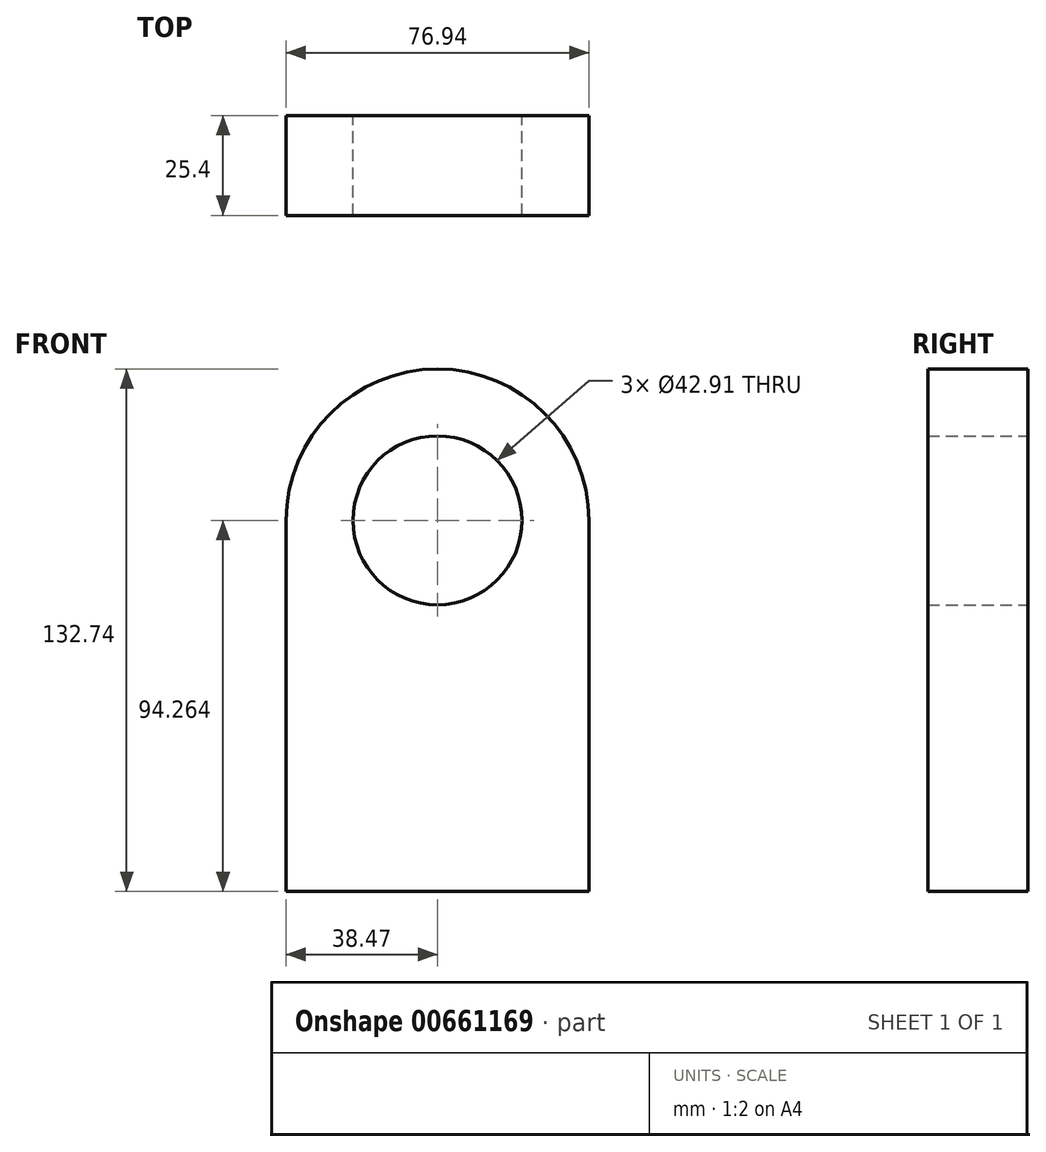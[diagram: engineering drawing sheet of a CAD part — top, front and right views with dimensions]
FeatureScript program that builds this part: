
annotation { "Feature Type Name" : "Feature", "Feature Type Description" : "" }
export const myFeature = defineFeature(function(context is Context, id is Id, definition is map)
    precondition{}
    {
        {
            var Q0;
            Q0=qCreatedBy(makeId("Front.planeOp"),FACE);
            var sketch = newSketch(context, id + "F0", { "sketchPlane" : qUnion([Q0])});
            skLineSegment(sketch, "E0.top", {"start": v(38.47, -47.13) * mm, "end": v(-38.47, -47.13) * mm});
            skLineSegment(sketch, "E0.left", {"start": v(38.47, 47.13) * mm, "end": v(38.47, -47.13) * mm});
            skLineSegment(sketch, "E0.right", {"start": v(-38.47, 47.13) * mm, "end": v(-38.47, -47.13) * mm});
            skPoint(sketch, "E0.middle", {"position": v(0, 0) * mm});
            skArc(sketch, "E1", {"start": v(38.47, 47.13) * mm, "mid": v(0, 85.6) * mm, "end": v(-38.47, 47.13) * mm});
            skCircle(sketch, "E2", {"center": v(0, 47.13) * mm, "radius": 21.45 * mm});
            skSolve(sketch);
        }
        {
            var Q0;
            Q0=qSketchRegion(id+"F0",true);
            extrude(context, id + "F1", {"entities" : qUnion([Q0]), "depth" : 25.4 * mm, "offsetDistance" : 25.4 * mm});
        }
    });
